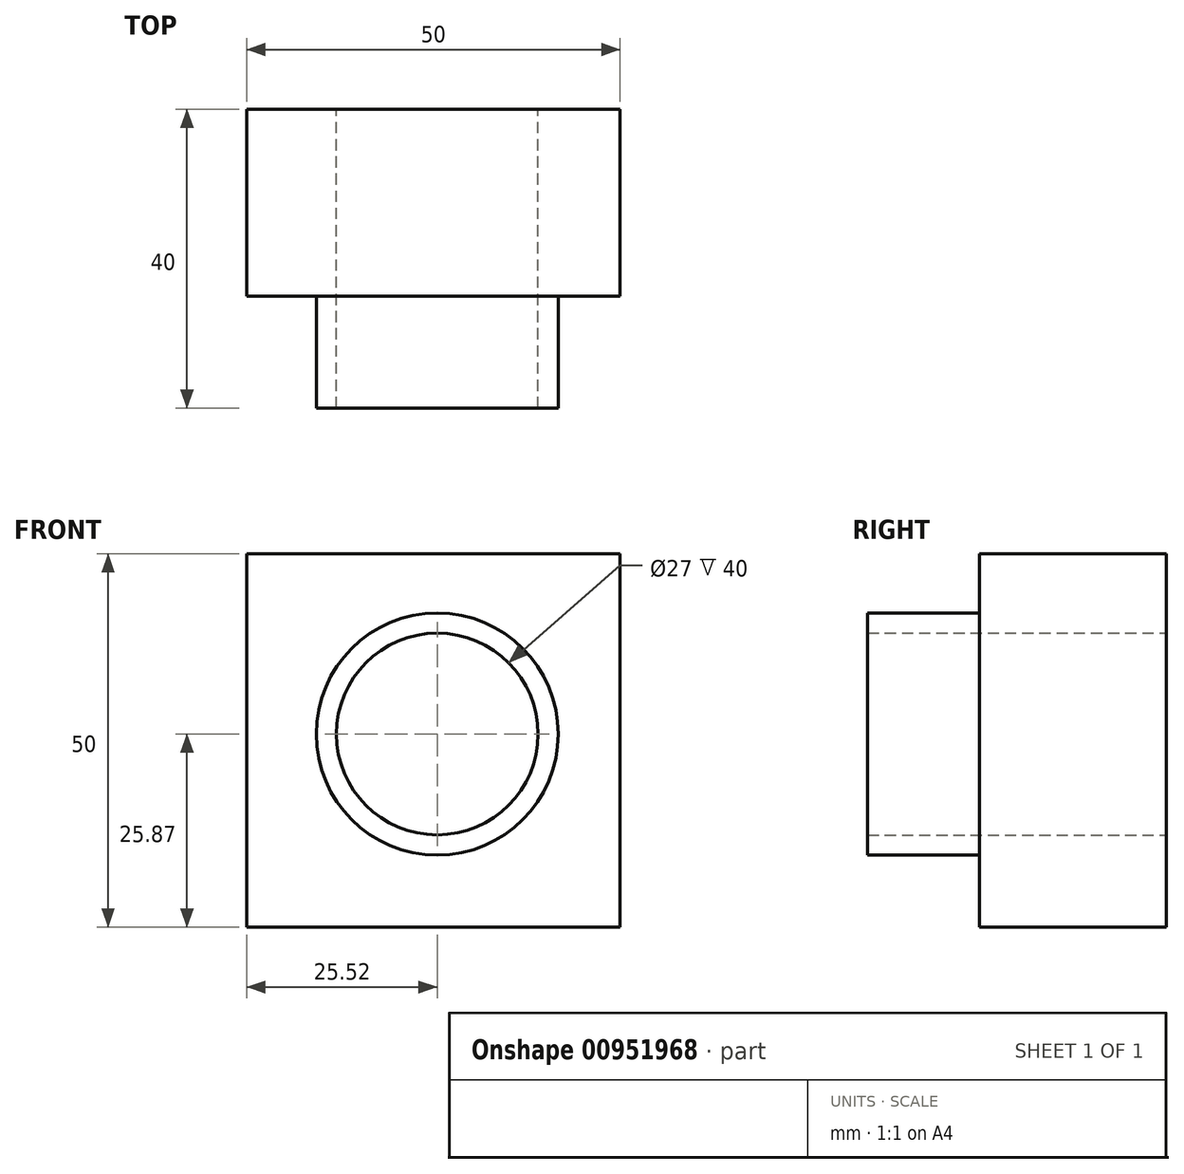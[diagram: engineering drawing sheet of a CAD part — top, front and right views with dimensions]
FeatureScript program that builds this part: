
annotation { "Feature Type Name" : "Feature", "Feature Type Description" : "" }
export const myFeature = defineFeature(function(context is Context, id is Id, definition is map)
    precondition{}
    {
        {
            var Q0;
            Q0=qCreatedBy(makeId("Front.planeOp"),FACE);
            var sketch = newSketch(context, id + "F0", { "sketchPlane" : qUnion([Q0])});
            skLineSegment(sketch, "E0.bottom", {"start": v(-25.52, 24.13) * mm, "end": v(24.48, 24.13) * mm});
            skLineSegment(sketch, "E0.top", {"start": v(-25.52, -25.87) * mm, "end": v(24.48, -25.87) * mm});
            skLineSegment(sketch, "E0.left", {"start": v(-25.52, 24.13) * mm, "end": v(-25.52, -25.87) * mm});
            skLineSegment(sketch, "E0.right", {"start": v(24.48, 24.13) * mm, "end": v(24.48, -25.87) * mm});
            skSolve(sketch);
        }
        {
            var Q0;
            Q0=makeQuery(id+"F0.imprint","IMPRINT",FACE,{"disambiguationData":[TD([[makeQuery(id+"F0.imprint","IMPRINT",EDGE,{"derivedFrom":sQuery(id+"F0.wireOp",EDGE,"E0.bottom")}),-1.0]])]});
            extrude(context, id + "F1", {"entities" : qUnion([Q0]), "depth" : 25 * mm, "offsetDistance" : 25 * mm});
        }
        {
            var Q0;
            Q0=qCreatedBy(makeId("Front.planeOp"),FACE);
            var sketch = newSketch(context, id + "F2", { "sketchPlane" : qUnion([Q0])});
            skCircle(sketch, "E1", {"center": v(0, 0) * mm, "radius": 16.2 * mm});
            skSolve(sketch);
        }
        {
            var Q0;
            Q0 = qSketchRegion(id + "F2", true);
            extrude(context, id + "F3", {"entities" : qUnion([Q0]), "operationType" : NewBodyOperationType.ADD, "depth" : 40 * mm, "offsetDistance" : 25 * mm});
        }
        {
            var Q0;
            Q0=qCreatedBy(makeId("Front.planeOp"),FACE);
            var sketch = newSketch(context, id + "F4", { "sketchPlane" : qUnion([Q0])});
            skCircle(sketch, "E2", {"center": v(0, 0) * mm, "radius": 13.5 * mm});
            skSolve(sketch);
        }
        {
            var Q0;
            Q0=makeQuery(id+"F4.imprint","IMPRINT",FACE,{"disambiguationData":[TD([[makeQuery(id+"F4.imprint","IMPRINT",EDGE,{"derivedFrom":sQuery(id+"F4.wireOp",EDGE,"E2")}),1.0]])]});
            extrude(context, id + "F5", {"entities" : qUnion([Q0]), "operationType" : NewBodyOperationType.REMOVE, "depth" : 40 * mm, "offsetDistance" : 25 * mm});
        }
    });
